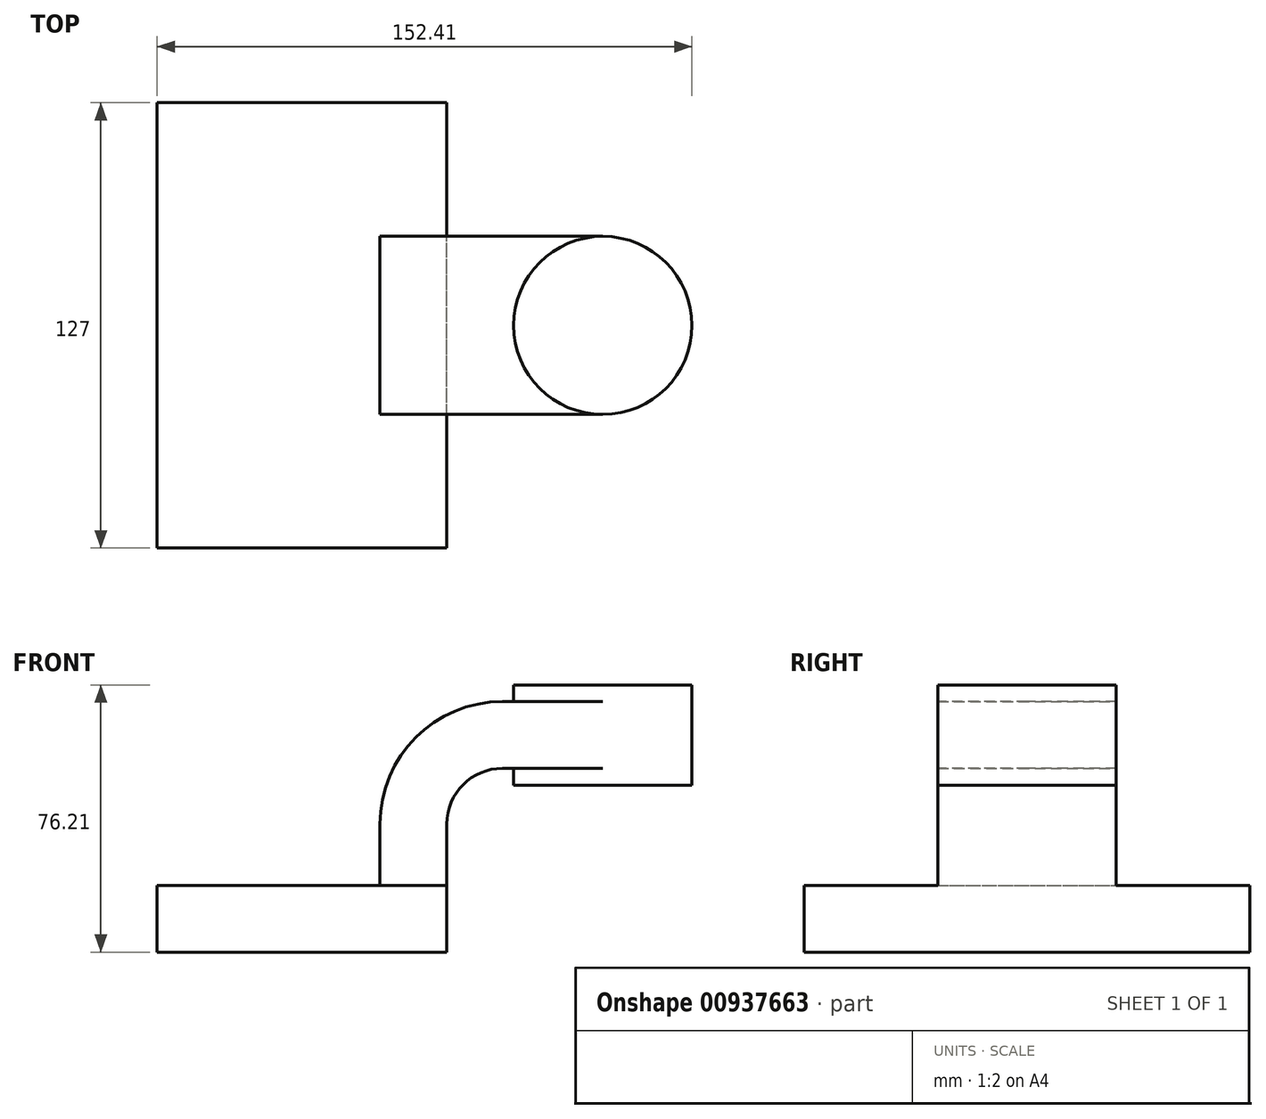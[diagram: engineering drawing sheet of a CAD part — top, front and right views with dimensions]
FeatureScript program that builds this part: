
annotation { "Feature Type Name" : "Feature", "Feature Type Description" : "" }
export const myFeature = defineFeature(function(context is Context, id is Id, definition is map)
    precondition{}
    {
        {
            var Q0;
            Q0=qCreatedBy(makeId("Front.planeOp"),FACE);
            var sketch = newSketch(context, id + "F0", { "sketchPlane" : qUnion([Q0])});
            skLineSegment(sketch, "E0.bottom", {"start": v(-41.28, 9.52) * mm, "end": v(41.28, 9.53) * mm});
            skLineSegment(sketch, "E0.top", {"start": v(-41.28, -9.53) * mm, "end": v(41.28, -9.53) * mm});
            skLineSegment(sketch, "E0.left", {"start": v(-41.28, 9.52) * mm, "end": v(-41.28, -9.53) * mm});
            skLineSegment(sketch, "E0.right", {"start": v(41.27, 9.53) * mm, "end": v(41.28, -9.52) * mm});
            skPoint(sketch, "E0.middle", {"position": v(0, 0) * mm});
            skLineSegment(sketch, "E1.bottom", {"start": v(111.12, 38.1) * mm, "end": v(60.32, 38.1) * mm});
            skLineSegment(sketch, "E1.top", {"start": v(111.12, 66.68) * mm, "end": v(60.32, 66.68) * mm});
            skLineSegment(sketch, "E1.left", {"start": v(111.12, 38.1) * mm, "end": v(111.12, 66.68) * mm});
            skLineSegment(sketch, "E1.right", {"start": v(60.32, 38.1) * mm, "end": v(60.32, 66.67) * mm});
            skPoint(sketch, "E1.middle", {"position": v(85.72, 52.39) * mm});
            skLineSegment(sketch, "E2", {"start": v(41.27, 9.53) * mm, "end": v(41.27, 27) * mm});
            skArc(sketch, "E3", {"start": v(41.27, 27) * mm, "mid": v(45.92, 38.23) * mm, "end": v(57.15, 42.88) * mm});
            skLineSegment(sketch, "E4", {"start": v(57.15, 42.88) * mm, "end": v(85.72, 42.88) * mm});
            skLineSegment(sketch, "E5.0", {"start": v(57.15, 61.93) * mm, "end": v(85.72, 61.93) * mm});
            skArc(sketch, "E5.1", {"start": v(22.22, 27) * mm, "mid": v(32.45, 51.7) * mm, "end": v(57.15, 61.93) * mm});
            skLineSegment(sketch, "E5.2", {"start": v(22.22, 9.53) * mm, "end": v(22.22, 27) * mm});
            skLineSegment(sketch, "E6", {"start": v(85.72, 38.1) * mm, "end": v(85.72, 66.68) * mm});
            skFitSpline(sketch, "E7", {"points": [v(-41.28, 9.53) * mm, v(30.08, 62.16) * mm, v(57.15, 61.93) * mm], "startDerivative": vector(163.07, 71.18) * mm, "endDerivative": vector(66.46, -5.35) * mm});
            skSolve(sketch);
        }
        {
            var Q0;
            Q0=makeQuery(id+"F0.imprint","IMPRINT",FACE,{"disambiguationData":[TD([[makeQuery(id+"F0.imprint","IMPRINT",EDGE,{"derivedFrom":sQuery(id+"F0.wireOp",EDGE,"E0.top")}),1.0]])]});
            extrude(context, id + "F1", {"entities" : qUnion([Q0]), "endBound" : BoundingType.SYMMETRIC, "depth" : 127 * mm, "offsetDistance" : 25.4 * mm});
        }
        {
            var Q0;
            {var subQ1=sQuery(id+"F0.wireOp",EDGE,"E2");Q0=makeQuery(id+"F0.imprint","IMPRINT",FACE,{"disambiguationData":[TD([[makeQuery(id+"F0.imprint","IMPRINT",EDGE,{"derivedFrom":subQ1}),1.0]])]});}
            var Q1;
            {var subQ0=sQuery(id+"F0.wireOp",EDGE,"E4");var subQ1=sQuery(id+"F0.wireOp",EDGE,"E1.right");var subQ2=makeQuery(id+"F0.imprint","INTERSECT",VERTEX,{"derivedFrom":[subQ1,subQ0]});Q1=makeQuery(id+"F0.imprint","IMPRINT",FACE,{"disambiguationData":[TD([[makeQuery(id+"F0.imprint","IMPRINT",EDGE,{"disambiguationData":[TD([[subQ2,-1.0]])],"derivedFrom":subQ1}),-1.0]])]});}
            extrude(context, id + "F2", {"entities" : qUnion([Q0, Q1]), "operationType" : NewBodyOperationType.ADD, "endBound" : BoundingType.SYMMETRIC, "depth" : 50.8 * mm, "offsetDistance" : 25.4 * mm});
        }
        {
            var Q0;
            Q0=makeQuery(id+"F0.imprint","IMPRINT",FACE,{"disambiguationData":[TD([[makeQuery(id+"F0.imprint","IMPRINT",EDGE,{"derivedFrom":sQuery(id+"F0.wireOp",EDGE,"E5.1")}),1.0]])]});
            extrude(context, id + "F3", {"entities" : qUnion([Q0]), "operationType" : NewBodyOperationType.ADD, "endBound" : BoundingType.SYMMETRIC, "depth" : 15.88 * mm, "offsetDistance" : 25.4 * mm});
        }
        {
            var Q0;
            {var subQ4=sQuery(id+"F0.wireOp",EDGE,"E1.left");Q0=makeQuery(id+"F0.imprint","IMPRINT",FACE,{"disambiguationData":[TD([[makeQuery(id+"F0.imprint","IMPRINT",EDGE,{"derivedFrom":subQ4}),1.0]])]});}
            var Q1;
            Q1=sQuery(id+"F0.wireOp",EDGE,"E6");
            revolve(context, id + "F4", {"operationType" : NewBodyOperationType.ADD, "surfaceOperationType" : NewSurfaceOperationType.NEW, "entities" : qUnion([Q0]), "axis" : qUnion([Q1]), "revolveType" : RevolveType.FULL});
        }
    });
